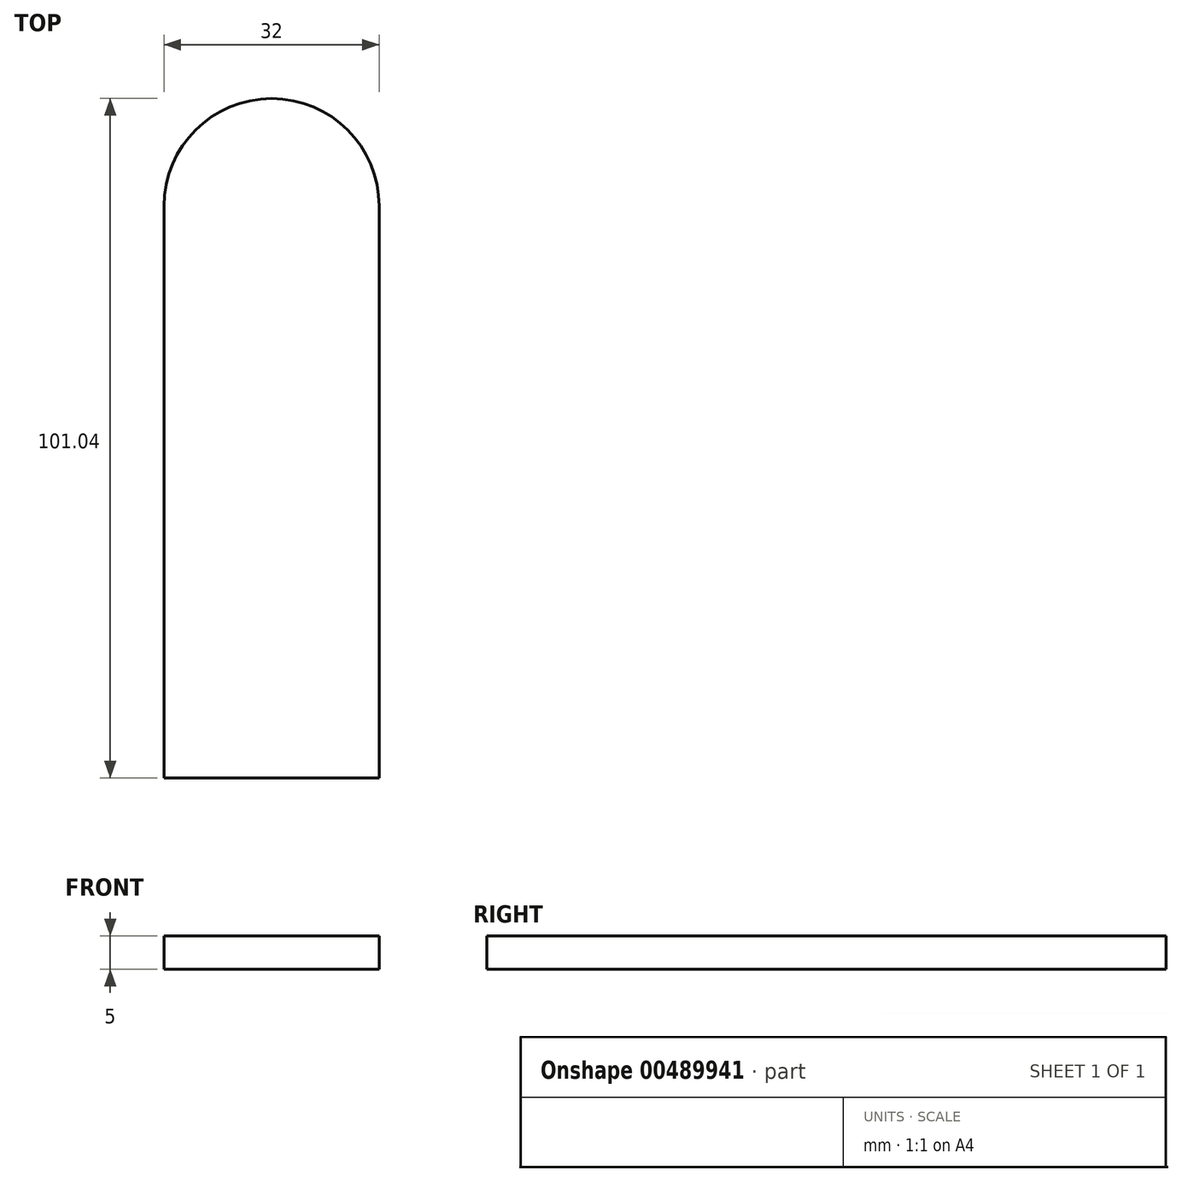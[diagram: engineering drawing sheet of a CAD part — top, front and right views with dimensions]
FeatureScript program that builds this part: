
annotation { "Feature Type Name" : "Feature", "Feature Type Description" : "" }
export const myFeature = defineFeature(function(context is Context, id is Id, definition is map)
    precondition{}
    {
        {
            var Q0;
            Q0=qCreatedBy(makeId("Top.planeOp"),FACE);
            var sketch = newSketch(context, id + "F0", { "sketchPlane" : qUnion([Q0])});
            skLineSegment(sketch, "E0.bottom", {"start": v(-56.88, 45.4) * mm, "end": v(-24.88, 45.4) * mm});
            skLineSegment(sketch, "E0.top", {"start": v(-56.88, -39.65) * mm, "end": v(-24.88, -39.65) * mm});
            skLineSegment(sketch, "E0.left", {"start": v(-56.88, 45.4) * mm, "end": v(-56.88, -39.65) * mm});
            skLineSegment(sketch, "E0.right", {"start": v(-24.88, 45.4) * mm, "end": v(-24.88, -39.65) * mm});
            skArc(sketch, "E1", {"start": v(-24.88, 45.4) * mm, "mid": v(-40.88, 61.39) * mm, "end": v(-56.88, 45.4) * mm});
            skSolve(sketch);
        }
        {
            var Q0;
            Q0=makeQuery(id+"F0.imprint","IMPRINT",FACE,{"disambiguationData":[TD([[makeQuery(id+"F0.imprint","IMPRINT",EDGE,{"derivedFrom":sQuery(id+"F0.wireOp",EDGE,"E0.bottom")}),-1.0]])]});
            var Q1;
            Q1=makeQuery(id+"F0.imprint","IMPRINT",FACE,{"disambiguationData":[TD([[makeQuery(id+"F0.imprint","IMPRINT",EDGE,{"derivedFrom":sQuery(id+"F0.wireOp",EDGE,"E0.bottom")}),1.0]])]});
            extrude(context, id + "F1", {"entities" : qUnion([Q0, Q1]), "depth" : 5 * mm});
        }
    });
